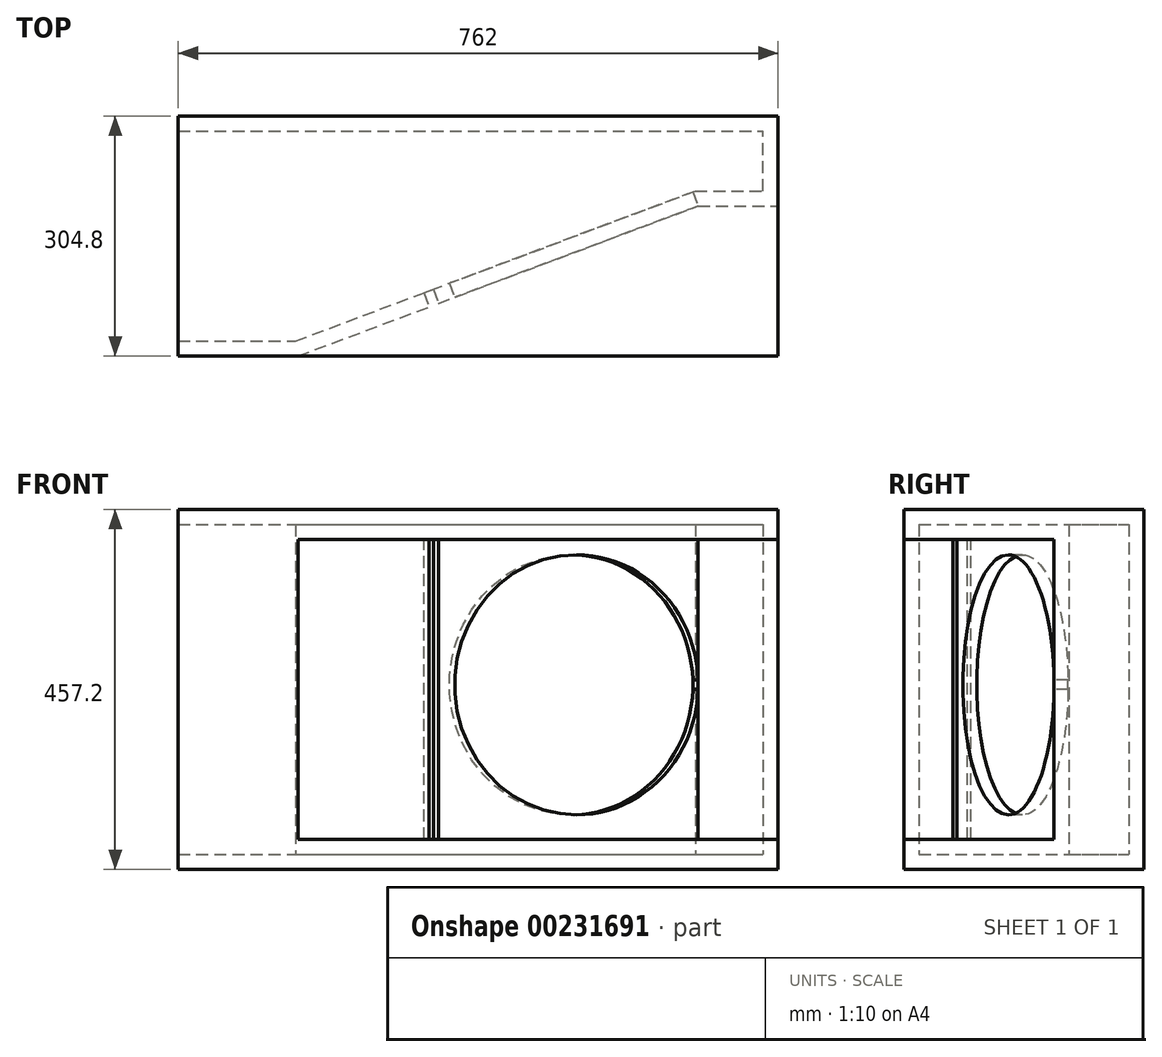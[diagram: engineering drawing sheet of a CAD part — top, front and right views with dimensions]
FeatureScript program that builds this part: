
annotation { "Feature Type Name" : "Feature", "Feature Type Description" : "" }
export const myFeature = defineFeature(function(context is Context, id is Id, definition is map)
    precondition{}
    {
        {
            var Q0;
            Q0=qCreatedBy(makeId("Front.planeOp"),FACE);
            var sketch = newSketch(context, id + "F0", { "sketchPlane" : qUnion([Q0])});
            skLineSegment(sketch, "E0.bottom", {"start": v(-762, 457.2) * mm, "end": v(0, 457.2) * mm});
            skLineSegment(sketch, "E0.top", {"start": v(-762, 0) * mm, "end": v(0, 0) * mm});
            skLineSegment(sketch, "E0.left", {"start": v(-762, 457.2) * mm, "end": v(-762, 0) * mm});
            skLineSegment(sketch, "E0.right", {"start": v(0, 457.2) * mm, "end": v(0, 0) * mm});
            skSolve(sketch);
        }
        {
            var Q0;
            Q0=makeQuery(id+"F0.imprint","IMPRINT",FACE,{"disambiguationData":[TD([[makeQuery(id+"F0.imprint","IMPRINT",EDGE,{"derivedFrom":sQuery(id+"F0.wireOp",EDGE,"E0.bottom")}),-1.0]])]});
            extrude(context, id + "F1", {"entities" : qUnion([Q0]), "depth" : 304.8 * mm});
        }
        {
            var Q0;
            Q0=makeQuery(id+"F1.opExtrude","SWEPT_FACE",FACE,{"disambiguationData":[OSD([sQuery(id+"F0.wireOp",EDGE,"E0.right")])]});
            var sketch = newSketch(context, id + "F2", { "sketchPlane" : qUnion([Q0])});
            skLineSegment(sketch, "E1.bottom", {"start": v(-304.8, 419.1) * mm, "end": v(-114.3, 419.1) * mm});
            skLineSegment(sketch, "E1.top", {"start": v(-304.8, 38.1) * mm, "end": v(-114.3, 38.1) * mm});
            skLineSegment(sketch, "E1.left", {"start": v(-304.8, 419.1) * mm, "end": v(-304.8, 38.1) * mm});
            skLineSegment(sketch, "E1.right", {"start": v(-114.3, 419.1) * mm, "end": v(-114.3, 38.1) * mm});
            skSolve(sketch);
        }
        {
            var Q0;
            Q0=makeQuery(id+"F2.imprint","IMPRINT",FACE,{"disambiguationData":[TD([[makeQuery(id+"F2.imprint","IMPRINT",EDGE,{"derivedFrom":sQuery(id+"F2.wireOp",EDGE,"E1.bottom")}),-1.0]])]});
            extrude(context, id + "F3", {"entities" : qUnion([Q0]), "operationType" : NewBodyOperationType.REMOVE, "oppositeDirection" : true, "depth" : 609.6 * mm});
        }
        {
            var Q0;
            Q0=makeQuery(id+"F3.boolean.opBoolean","COPY",FACE,{"derivedFrom":makeQuery(id+"F3.opExtrude","SWEPT_FACE",FACE,{"disambiguationData":[OSD([sQuery(id+"F2.wireOp",EDGE,"E1.top")])]})});
            var sketch = newSketch(context, id + "F4", { "sketchPlane" : qUnion([Q0])});
            skLineSegment(sketch, "E2.bottom", {"start": v(-609.6, -114.3) * mm, "end": v(0, -114.3) * mm});
            skLineSegment(sketch, "E2.top", {"start": v(-609.6, -304.8) * mm, "end": v(0, -304.8) * mm});
            skLineSegment(sketch, "E2.left", {"start": v(-609.6, -114.3) * mm, "end": v(-609.6, -304.8) * mm});
            skLineSegment(sketch, "E2.right", {"start": v(0, -114.3) * mm, "end": v(0, -304.8) * mm});
            skSolve(sketch);
        }
        {
            var Q0;
            Q0=makeQuery(id+"F4.imprint","IMPRINT",FACE,{"disambiguationData":[TD([[makeQuery(id+"F4.imprint","IMPRINT",EDGE,{"derivedFrom":sQuery(id+"F4.wireOp",EDGE,"E2.bottom")}),-1.0]])]});
            var sketch = newSketch(context, id + "F5", { "sketchPlane" : qUnion([Q0])});
            skLineSegment(sketch, "E3", {"start": v(-609.6, -76.2) * mm, "end": v(0, -76.2) * mm});
            skLineSegment(sketch, "E4", {"start": v(-609.6, -76.2) * mm, "end": v(-609.6, -304.8) * mm});
            skLineSegment(sketch, "E5", {"start": v(-609.6, -304.8) * mm, "end": v(0, -76.2) * mm});
            skSolve(sketch);
        }
        {
            var Q0;
            {var subQ0=sQuery(id+"F5.wireOp",EDGE,"E4");var subQ1=makeQuery(id+"F4.imprint","IMPRINT",EDGE,{"derivedFrom":sQuery(id+"F4.wireOp",EDGE,"E2.bottom")});var subQ2=makeQuery(id+"F5.imprint","INTERSECT",VERTEX,{"derivedFrom":[subQ1,subQ0]});Q0=makeQuery(id+"F5.imprint","IMPRINT",FACE,{"disambiguationData":[TD([[makeQuery(id+"F5.imprint","IMPRINT",EDGE,{"disambiguationData":[TD([[subQ2,-1.0]])],"derivedFrom":subQ1}),-1.0]])]});}
            var Q1;
            Q1=makeQuery(id+"F1.opExtrude","SWEPT_FACE",FACE,{"disambiguationData":[OSD([sQuery(id+"F0.wireOp",EDGE,"E0.bottom")])]});
            extrude(context, id + "F6", {"entities" : qUnion([Q0]), "operationType" : NewBodyOperationType.ADD, "endBound" : BoundingType.UP_TO_SURFACE, "endBoundEntityFace" : qUnion([Q1]), "depth" : 31.75 * mm});
        }
        {
            var Q0;
            Q0=makeQuery(id+"F6.opExtrude","SWEPT_FACE",FACE,{"disambiguationData":[OSD([sQuery(id+"F5.wireOp",EDGE,"E5")])]});
            var sketch = newSketch(context, id + "F7", { "sketchPlane" : qUnion([Q0])});
            skCircle(sketch, "E6", {"center": v(-300.36, 234.55) * mm, "radius": 165.2 * mm});
            skPoint(sketch, "E6.first.point", {"position": v(-135.26, 228.6) * mm});
            skPoint(sketch, "E6.second.point", {"position": v(-465.46, 228.6) * mm});
            skPoint(sketch, "E6.second.point.positionSnap0", {"position": v(-135.26, 228.6) * mm});
            skPoint(sketch, "E6.third.point", {"position": v(-344.67, 393.7) * mm});
            skSolve(sketch);
        }
        {
            var Q0;
            Q0=makeQuery(id+"F1.opExtrude","SWEPT_FACE",FACE,{"disambiguationData":[OSD([sQuery(id+"F0.wireOp",EDGE,"E0.left")])]});
            shell(context, id + "F8", {"entities" : qUnion([Q0]), "thickness" : 19.05 * mm});
        }
        {
            var Q0;
            {var subQ0=sQuery(id+"F7.wireOp",EDGE,"E6");var subQ1=makeQuery(id+"F6.opExtrude","SWEPT_EDGE",EDGE,{"disambiguationData":[OSD([sQuery(id+"F4.wireOp",EDGE,"E2.bottom"),sQuery(id+"F5.wireOp",EDGE,"E5")])]});var subQ2=makeQuery(id+"F7.imprint","INTERSECT",VERTEX,{"disambiguationData":[OD(0.0)],"derivedFrom":[subQ1,subQ0]});Q0=makeQuery(id+"F7.imprint","IMPRINT",FACE,{"disambiguationData":[TD([[makeQuery(id+"F7.imprint","IMPRINT",EDGE,{"disambiguationData":[TD([[subQ2,-1.0]])],"derivedFrom":subQ0}),1.0]])]});}
            extrude(context, id + "F9", {"entities" : qUnion([Q0]), "operationType" : NewBodyOperationType.REMOVE, "oppositeDirection" : true, "depth" : 25.4 * mm});
        }
        {
            var Q0;
            Q0=makeQuery(id+"F6.opExtrude","SWEPT_FACE",FACE,{"disambiguationData":[OSD([sQuery(id+"F5.wireOp",EDGE,"E5")])]});
            var sketch = newSketch(context, id + "F10", { "sketchPlane" : qUnion([Q0])});
            skLineSegment(sketch, "E7", {"start": v(-487.3, 419.1) * mm, "end": v(-487.3, 38.1) * mm});
            skPoint(sketch, "E7.endSnap0", {"position": v(-487.3, 233.03) * mm});
            skSolve(sketch);
        }
        {
            var Q0;
            {var subQ0=sQuery(id+"F10.wireOp",EDGE,"E7");Q0=makeQuery(id+"F10.imprint","IMPRINT",FACE,{"disambiguationData":[TD([[makeQuery(id+"F10.imprint","IMPRINT",EDGE,{"derivedFrom":subQ0}),-1.0]])]});}
            var sketch = newSketch(context, id + "F11", { "sketchPlane" : qUnion([Q0])});
            skLineSegment(sketch, "E8", {"start": v(-500, 419.1) * mm, "end": v(-500, 38.1) * mm});
            skSolve(sketch);
        }
        {
            var Q0;
            {var subQ0=sQuery(id+"F11.wireOp",EDGE,"E8");Q0=makeQuery(id+"F11.imprint","IMPRINT",FACE,{"disambiguationData":[TD([[makeQuery(id+"F11.imprint","IMPRINT",EDGE,{"derivedFrom":subQ0}),1.0]])]});}
            extrude(context, id + "F12", {"entities" : qUnion([Q0]), "operationType" : NewBodyOperationType.REMOVE, "oppositeDirection" : true, "depth" : 25.4 * mm});
        }
    });
